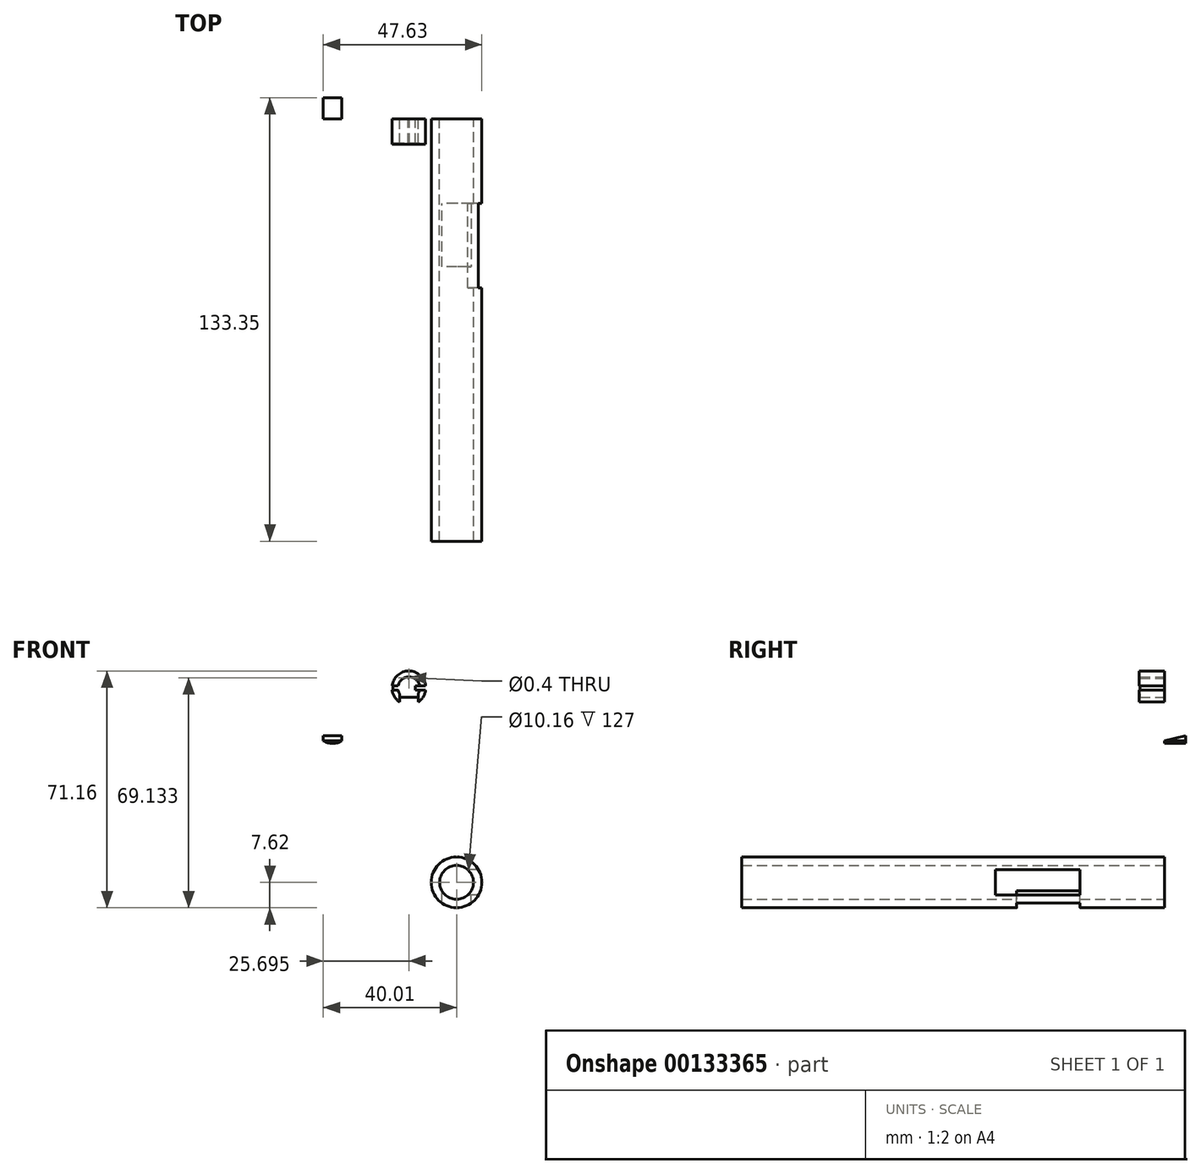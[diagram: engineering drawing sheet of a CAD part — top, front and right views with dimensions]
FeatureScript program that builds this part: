
annotation { "Feature Type Name" : "Feature", "Feature Type Description" : "" }
export const myFeature = defineFeature(function(context is Context, id is Id, definition is map)
    precondition{}
    {
        {
            var Q0;
            Q0=qCreatedBy(makeId("Front.planeOp"),FACE);
            var sketch = newSketch(context, id + "F0", { "sketchPlane" : qUnion([Q0])});
            skCircle(sketch, "E0", {"center": v(0, 0) * mm, "radius": 7.62 * mm});
            skCircle(sketch, "E1", {"center": v(0, 0) * mm, "radius": 5.08 * mm});
            skCircle(sketch, "E2", {"center": v(-37.21, 46.83) * mm, "radius": 5.08 * mm});
            skCircle(sketch, "E3", {"center": v(-37.21, 46.83) * mm, "radius": 2.8 * mm});
            skLineSegment(sketch, "E4", {"start": v(-37.21, 46.83) * mm, "end": v(-37.21, 41.75) * mm, "construction": true});
            skLineSegment(sketch, "E5", {"start": v(-37.21, 41.75) * mm, "end": v(-37.21, 46.83) * mm, "construction": true});
            skLineSegment(sketch, "E6", {"start": v(-37.21, 46.83) * mm, "end": v(-37.21, 51.9) * mm, "construction": true});
            skLineSegment(sketch, "E7", {"start": v(-32.13, 46.83) * mm, "end": v(-42.3, 46.83) * mm, "construction": true});
            skLineSegment(sketch, "E8", {"start": v(-34.42, 46.83) * mm, "end": v(-34.42, 42.58) * mm});
            skLineSegment(sketch, "E9", {"start": v(-40, 46.83) * mm, "end": v(-40, 42.58) * mm});
            skLineSegment(sketch, "E10", {"start": v(-37.21, 44.03) * mm, "end": v(-40, 44.03) * mm});
            skLineSegment(sketch, "E11", {"start": v(-40, 44.03) * mm, "end": v(-34.42, 44.03) * mm});
            skCircle(sketch, "E12", {"center": v(22.9, 11.64) * mm, "radius": 7.62 * mm});
            skCircle(sketch, "E13", {"center": v(22.9, 11.64) * mm, "radius": 5.08 * mm});
            skCircle(sketch, "E14", {"center": v(-14.31, 58.46) * mm, "radius": 5.08 * mm});
            skCircle(sketch, "E15", {"center": v(-14.31, 58.46) * mm, "radius": 2.8 * mm});
            skLineSegment(sketch, "E16", {"start": v(-14.31, 58.46) * mm, "end": v(-14.31, 53.38) * mm, "construction": true});
            skLineSegment(sketch, "E17", {"start": v(-14.31, 53.38) * mm, "end": v(-14.31, 58.46) * mm, "construction": true});
            skLineSegment(sketch, "E18", {"start": v(-14.31, 58.46) * mm, "end": v(-14.31, 63.54) * mm, "construction": true});
            skLineSegment(sketch, "E19", {"start": v(-9.23, 58.46) * mm, "end": v(-19.4, 58.46) * mm, "construction": true});
            skLineSegment(sketch, "E20", {"start": v(-11.52, 58.46) * mm, "end": v(-11.52, 54.22) * mm});
            skLineSegment(sketch, "E21", {"start": v(-17.1, 58.46) * mm, "end": v(-17.1, 54.22) * mm});
            skLineSegment(sketch, "E22", {"start": v(-14.31, 55.67) * mm, "end": v(-17.1, 55.67) * mm});
            skLineSegment(sketch, "E23", {"start": v(-17.1, 55.67) * mm, "end": v(-11.52, 55.67) * mm});
            skCircle(sketch, "E24", {"center": v(-14.31, 58.46) * mm, "radius": 3.3 * mm});
            skPoint(sketch, "E25", {"position": v(-12.4, 58.46) * mm});
            skLineSegment(sketch, "E26", {"start": v(-12.4, 58.46) * mm, "end": v(-12.4, 59.1) * mm});
            skLineSegment(sketch, "E27", {"start": v(-12.4, 59.1) * mm, "end": v(-9.27, 59.1) * mm});
            skLineSegment(sketch, "E28.MirrorCS", {"start": v(-12.4, 57.83) * mm, "end": v(-9.27, 57.83) * mm});
            skLineSegment(sketch, "E29.MirrorCS", {"start": v(-12.4, 58.46) * mm, "end": v(-12.4, 57.83) * mm});
            skLineSegment(sketch, "E30.MirrorCS", {"start": v(-16.22, 59.1) * mm, "end": v(-19.36, 59.1) * mm});
            skLineSegment(sketch, "E31.MirrorCS", {"start": v(-16.22, 58.46) * mm, "end": v(-16.22, 59.1) * mm});
            skLineSegment(sketch, "E32.MirrorCS", {"start": v(-16.22, 58.46) * mm, "end": v(-16.22, 57.83) * mm});
            skLineSegment(sketch, "E33.MirrorCS", {"start": v(-16.22, 57.83) * mm, "end": v(-19.36, 57.83) * mm});
            skPoint(sketch, "E34", {"position": v(-19.36, 59.1) * mm});
            skPoint(sketch, "E35", {"position": v(-19.1, 59.1) * mm});
            skLineSegment(sketch, "E36", {"start": v(-19.1, 59.1) * mm, "end": v(-19.1, 57.83) * mm});
            skLineSegment(sketch, "E37", {"start": v(-14.31, 61.77) * mm, "end": v(-14.31, 61.26) * mm, "construction": true});
            skPoint(sketch, "E38", {"position": v(-14.31, 61.51) * mm});
            skCircle(sketch, "E39", {"center": v(-14.31, 61.51) * mm, "radius": 0.2 * mm});
            skSolve(sketch);
        }
        {
            var Q0;
            Q0=makeQuery(id+"F0.imprint","IMPRINT",FACE,{"disambiguationData":[TD([[makeQuery(id+"F0.imprint","IMPRINT",EDGE,{"derivedFrom":sQuery(id+"F0.wireOp",EDGE,"E0")}),1.0]])]});
            extrude(context, id + "F1", {"entities" : qUnion([Q0]), "depth" : 127 * mm});
        }
        {
            var Q0;
            Q0=qCreatedBy(makeId("Top.planeOp"),FACE);
            var sketch = newSketch(context, id + "F2", { "sketchPlane" : qUnion([Q0])});
            skLineSegment(sketch, "E40.bottom", {"start": v(4.44, -44.45) * mm, "end": v(-4.45, -44.45) * mm});
            skLineSegment(sketch, "E40.top", {"start": v(4.45, -25.4) * mm, "end": v(-4.45, -25.4) * mm});
            skLineSegment(sketch, "E40.left", {"start": v(4.44, -44.45) * mm, "end": v(4.45, -25.4) * mm});
            skLineSegment(sketch, "E40.right", {"start": v(-4.45, -44.45) * mm, "end": v(-4.45, -25.4) * mm});
            skPoint(sketch, "E40.middle", {"position": v(0, -34.93) * mm});
            skPoint(sketch, "E41", {"position": v(0, -127) * mm});
            skSolve(sketch);
        }
        {
            var Q0;
            Q0=makeQuery(id+"F2.imprint","IMPRINT",FACE,{"disambiguationData":[TD([[makeQuery(id+"F2.imprint","IMPRINT",EDGE,{"derivedFrom":sQuery(id+"F2.wireOp",EDGE,"E40.bottom")}),-1.0]])]});
            extrude(context, id + "F3", {"entities" : qUnion([Q0]), "operationType" : NewBodyOperationType.REMOVE, "oppositeDirection" : true, "depth" : 25.4 * mm});
        }
        {
            var Q0;
            Q0=qCreatedBy(makeId("Right.planeOp"),FACE);
            var sketch = newSketch(context, id + "F4", { "sketchPlane" : qUnion([Q0])});
            skPoint(sketch, "E42", {"position": v(-25.4, 0) * mm});
            skPoint(sketch, "E43", {"position": v(-50.8, 0) * mm});
            skLineSegment(sketch, "E44", {"start": v(-25.4, 0) * mm, "end": v(-25.4, 3.81) * mm});
            skLineSegment(sketch, "E45", {"start": v(-50.8, 0) * mm, "end": v(-50.8, 3.8) * mm});
            skLineSegment(sketch, "E46", {"start": v(-50.8, 3.81) * mm, "end": v(-25.4, 3.81) * mm});
            skLineSegment(sketch, "E47.MirrorCS", {"start": v(-50.8, 0) * mm, "end": v(-50.8, -3.8) * mm});
            skLineSegment(sketch, "E48.MirrorCS", {"start": v(-50.8, -3.81) * mm, "end": v(-25.4, -3.81) * mm});
            skLineSegment(sketch, "E49.MirrorCS", {"start": v(-25.4, 0) * mm, "end": v(-25.4, -3.81) * mm});
            skSolve(sketch);
        }
        {
            var Q0;
            Q0=makeQuery(id+"F4.imprint","IMPRINT",FACE,{"disambiguationData":[TD([[makeQuery(id+"F4.imprint","IMPRINT",EDGE,{"derivedFrom":sQuery(id+"F4.wireOp",EDGE,"E44")}),1.0]])]});
            extrude(context, id + "F5", {"entities" : qUnion([Q0]), "operationType" : NewBodyOperationType.REMOVE, "depth" : 25.4 * mm});
        }
        {
            var Q0;
            {var subQ4=sQuery(id+"F0.wireOp",EDGE,"E2");var subQ6=sQuery(id+"F0.wireOp",EDGE,"E8");var subQ7=makeQuery(id+"F0.imprint","INTERSECT",VERTEX,{"derivedFrom":[subQ4,subQ6]});Q0=makeQuery(id+"F0.imprint","IMPRINT",FACE,{"disambiguationData":[TD([[makeQuery(id+"F0.imprint","IMPRINT",EDGE,{"disambiguationData":[TD([[subQ7,1.0]])],"derivedFrom":subQ4}),1.0]])]});}
            extrude(context, id + "F6", {"entities" : qUnion([Q0]), "oppositeDirection" : true, "depth" : 6.35 * mm});
        }
        {
            var Q0;
            Q0=makeQuery(id+"F6.opExtrude","SWEPT_FACE",FACE,{"disambiguationData":[OSD([sQuery(id+"F0.wireOp",EDGE,"E9")])]});
            var sketch = newSketch(context, id + "F7", { "sketchPlane" : qUnion([Q0])});
            skLineSegment(sketch, "E50", {"start": v(-6.35, 44.03) * mm, "end": v(0, 42.58) * mm});
            skLineSegment(sketch, "E51", {"start": v(0, 42.58) * mm, "end": v(0, 44.03) * mm});
            skLineSegment(sketch, "E52", {"start": v(0, 44.03) * mm, "end": v(-6.35, 44.03) * mm});
            skSolve(sketch);
        }
        {
            var Q0;
            Q0=makeQuery(id+"F7.imprint","IMPRINT",FACE,{"disambiguationData":[TD([[makeQuery(id+"F7.imprint","IMPRINT",EDGE,{"derivedFrom":sQuery(id+"F7.wireOp",EDGE,"E50")}),1.0]])]});
            extrude(context, id + "F8", {"entities" : qUnion([Q0]), "operationType" : NewBodyOperationType.REMOVE, "oppositeDirection" : true, "depth" : 25.4 * mm});
        }
        {
            var Q0;
            {var subQ1=sQuery(id+"F0.wireOp",EDGE,"E21");var subQ5=sQuery(id+"F0.wireOp",EDGE,"E14");var subQ6=makeQuery(id+"F0.imprint","INTERSECT",VERTEX,{"derivedFrom":[subQ5,subQ1]});Q0=makeQuery(id+"F0.imprint","IMPRINT",FACE,{"disambiguationData":[TD([[makeQuery(id+"F0.imprint","IMPRINT",EDGE,{"disambiguationData":[TD([[subQ6,1.0]])],"derivedFrom":subQ5}),1.0]])]});}
            var Q1;
            {var subQ0=sQuery(id+"F0.wireOp",EDGE,"E20");var subQ1=sQuery(id+"F0.wireOp",EDGE,"E14");var subQ2=makeQuery(id+"F0.imprint","INTERSECT",VERTEX,{"derivedFrom":[subQ1,subQ0]});Q1=makeQuery(id+"F0.imprint","IMPRINT",FACE,{"disambiguationData":[TD([[makeQuery(id+"F0.imprint","IMPRINT",EDGE,{"disambiguationData":[TD([[subQ2,-1.0]])],"derivedFrom":subQ1}),1.0]])]});}
            var Q2;
            {var subQ0=sQuery(id+"F0.wireOp",EDGE,"E27");var subQ1=sQuery(id+"F0.wireOp",EDGE,"E14");var subQ2=makeQuery(id+"F0.imprint","INTERSECT",VERTEX,{"derivedFrom":[subQ1,subQ0]});Q2=makeQuery(id+"F0.imprint","IMPRINT",FACE,{"disambiguationData":[TD([[makeQuery(id+"F0.imprint","IMPRINT",EDGE,{"disambiguationData":[TD([[subQ2,-1.0]])],"derivedFrom":subQ1}),1.0]])]});}
            extrude(context, id + "F9", {"entities" : qUnion([Q0, Q1, Q2]), "depth" : 7.62 * mm});
        }
        {
            var Q0;
            {var subQ0=sQuery(id+"F0.wireOp",EDGE,"E23");var subQ1=sQuery(id+"F0.wireOp",EDGE,"E20");var subQ2=makeQuery(id+"F0.imprint","INTERSECT",VERTEX,{"derivedFrom":[subQ1,subQ0]});Q0=makeQuery(id+"F0.imprint","IMPRINT",FACE,{"disambiguationData":[TD([[makeQuery(id+"F0.imprint","IMPRINT",EDGE,{"disambiguationData":[TD([[subQ2,1.0]])],"derivedFrom":subQ1}),-1.0]])]});}
            var Q1;
            {var subQ0=sQuery(id+"F0.wireOp",EDGE,"E23");var subQ1=sQuery(id+"F0.wireOp",EDGE,"E21");var subQ2=makeQuery(id+"F0.imprint","INTERSECT",VERTEX,{"derivedFrom":[subQ1,subQ0]});Q1=makeQuery(id+"F0.imprint","IMPRINT",FACE,{"disambiguationData":[TD([[makeQuery(id+"F0.imprint","IMPRINT",EDGE,{"disambiguationData":[TD([[subQ2,1.0]])],"derivedFrom":subQ1}),1.0]])]});}
            var Q2;
            {var subQ0=sQuery(id+"F0.wireOp",EDGE,"E21");var subQ1=sQuery(id+"F0.wireOp",EDGE,"E15");var subQ2=makeQuery(id+"F0.imprint","INTERSECT",VERTEX,{"derivedFrom":[subQ1,subQ0]});Q2=makeQuery(id+"F0.imprint","IMPRINT",FACE,{"disambiguationData":[TD([[makeQuery(id+"F0.imprint","IMPRINT",EDGE,{"disambiguationData":[TD([[subQ2,-1.0]])],"derivedFrom":subQ1}),-1.0]])]});}
            var Q3;
            {var subQ5=sQuery(id+"F0.wireOp",EDGE,"E20");var subQ6=sQuery(id+"F0.wireOp",EDGE,"E14");var subQ7=makeQuery(id+"F0.imprint","INTERSECT",VERTEX,{"derivedFrom":[subQ6,subQ5]});Q3=makeQuery(id+"F0.imprint","IMPRINT",FACE,{"disambiguationData":[TD([[makeQuery(id+"F0.imprint","IMPRINT",EDGE,{"disambiguationData":[TD([[subQ7,-1.0]])],"derivedFrom":subQ6}),1.0]])]});}
            var Q4;
            Q4=makeQuery(id+"F9.opExtrude","CAP_FACE",FACE,{"disambiguationData":[OSD([sQuery(id+"F0.wireOp",EDGE,"E14"),sQuery(id+"F0.wireOp",EDGE,"E20"),sQuery(id+"F0.wireOp",EDGE,"E21"),sQuery(id+"F0.wireOp",EDGE,"E24")])],"isStart":true});
            var Q5;
            {var subQ3=sQuery(id+"F0.wireOp",EDGE,"E23");var subQ5=sQuery(id+"F0.wireOp",EDGE,"E15");var subQ6=makeQuery(id+"F0.imprint","INTERSECT",VERTEX,{"derivedFrom":[subQ5,subQ3]});Q5=makeQuery(id+"F0.imprint","IMPRINT",FACE,{"disambiguationData":[TD([[makeQuery(id+"F0.imprint","IMPRINT",EDGE,{"disambiguationData":[TD([[subQ6,-1.0]])],"derivedFrom":subQ5}),-1.0]])]});}
            var Q6;
            {var subQ0=sQuery(id+"F0.wireOp",EDGE,"E26");Q6=makeQuery(id+"F0.imprint","IMPRINT",FACE,{"disambiguationData":[TD([[makeQuery(id+"F0.imprint","IMPRINT",EDGE,{"derivedFrom":subQ0}),1.0]])]});}
            var Q7;
            {var subQ0=sQuery(id+"F0.wireOp",EDGE,"E28.MirrorCS");var subQ1=sQuery(id+"F0.wireOp",EDGE,"E20");var subQ2=makeQuery(id+"F0.imprint","INTERSECT",VERTEX,{"derivedFrom":[subQ1,subQ0]});Q7=makeQuery(id+"F0.imprint","IMPRINT",FACE,{"disambiguationData":[TD([[makeQuery(id+"F0.imprint","IMPRINT",EDGE,{"disambiguationData":[TD([[subQ2,-1.0]])],"derivedFrom":subQ1}),1.0]])]});}
            var Q8;
            {var subQ0=sQuery(id+"F0.wireOp",EDGE,"E21");var subQ1=sQuery(id+"F0.wireOp",EDGE,"E15");var subQ2=makeQuery(id+"F0.imprint","INTERSECT",VERTEX,{"derivedFrom":[subQ1,subQ0]});Q8=makeQuery(id+"F0.imprint","IMPRINT",FACE,{"disambiguationData":[TD([[makeQuery(id+"F0.imprint","IMPRINT",EDGE,{"disambiguationData":[TD([[subQ2,1.0]])],"derivedFrom":subQ1}),-1.0]])]});}
            var Q9;
            {var subQ0=sQuery(id+"F0.wireOp",EDGE,"E31.MirrorCS");Q9=makeQuery(id+"F0.imprint","IMPRINT",FACE,{"disambiguationData":[TD([[makeQuery(id+"F0.imprint","IMPRINT",EDGE,{"derivedFrom":subQ0}),1.0]])]});}
            var Q10;
            {var subQ0=sQuery(id+"F0.wireOp",EDGE,"E27");var subQ1=sQuery(id+"F0.wireOp",EDGE,"E15");var subQ2=makeQuery(id+"F0.imprint","INTERSECT",VERTEX,{"derivedFrom":[subQ1,subQ0]});Q10=makeQuery(id+"F0.imprint","IMPRINT",FACE,{"disambiguationData":[TD([[makeQuery(id+"F0.imprint","IMPRINT",EDGE,{"disambiguationData":[TD([[subQ2,-1.0]])],"derivedFrom":subQ1}),-1.0]])]});}
            var Q11;
            {var subQ5=sQuery(id+"F0.wireOp",EDGE,"E15");var subQ7=sQuery(id+"F0.wireOp",EDGE,"E33.MirrorCS");var subQ9=makeQuery(id+"F0.imprint","INTERSECT",VERTEX,{"derivedFrom":[subQ5,subQ7]});Q11=makeQuery(id+"F0.imprint","IMPRINT",FACE,{"disambiguationData":[TD([[makeQuery(id+"F0.imprint","IMPRINT",EDGE,{"disambiguationData":[TD([[subQ9,-1.0]])],"derivedFrom":subQ5}),-1.0]])]});}
            var Q12;
            {var subQ0=sQuery(id+"F0.wireOp",EDGE,"E33.MirrorCS");var subQ1=sQuery(id+"F0.wireOp",EDGE,"E21");var subQ2=makeQuery(id+"F0.imprint","INTERSECT",VERTEX,{"derivedFrom":[subQ1,subQ0]});Q12=makeQuery(id+"F0.imprint","IMPRINT",FACE,{"disambiguationData":[TD([[makeQuery(id+"F0.imprint","IMPRINT",EDGE,{"disambiguationData":[TD([[subQ2,-1.0]])],"derivedFrom":subQ1}),-1.0]])]});}
            var Q13;
            {var subQ5=sQuery(id+"F0.wireOp",EDGE,"E36");Q13=makeQuery(id+"F0.imprint","IMPRINT",FACE,{"disambiguationData":[TD([[makeQuery(id+"F0.imprint","IMPRINT",EDGE,{"derivedFrom":subQ5}),1.0]])]});}
            extrude(context, id + "F10", {"entities" : qUnion([Q0, Q1, Q2, Q3, Q4, Q5, Q6, Q7, Q8, Q9, Q10, Q11, Q12, Q13]), "operationType" : NewBodyOperationType.ADD, "depth" : 7.37 * mm});
        }
    });
